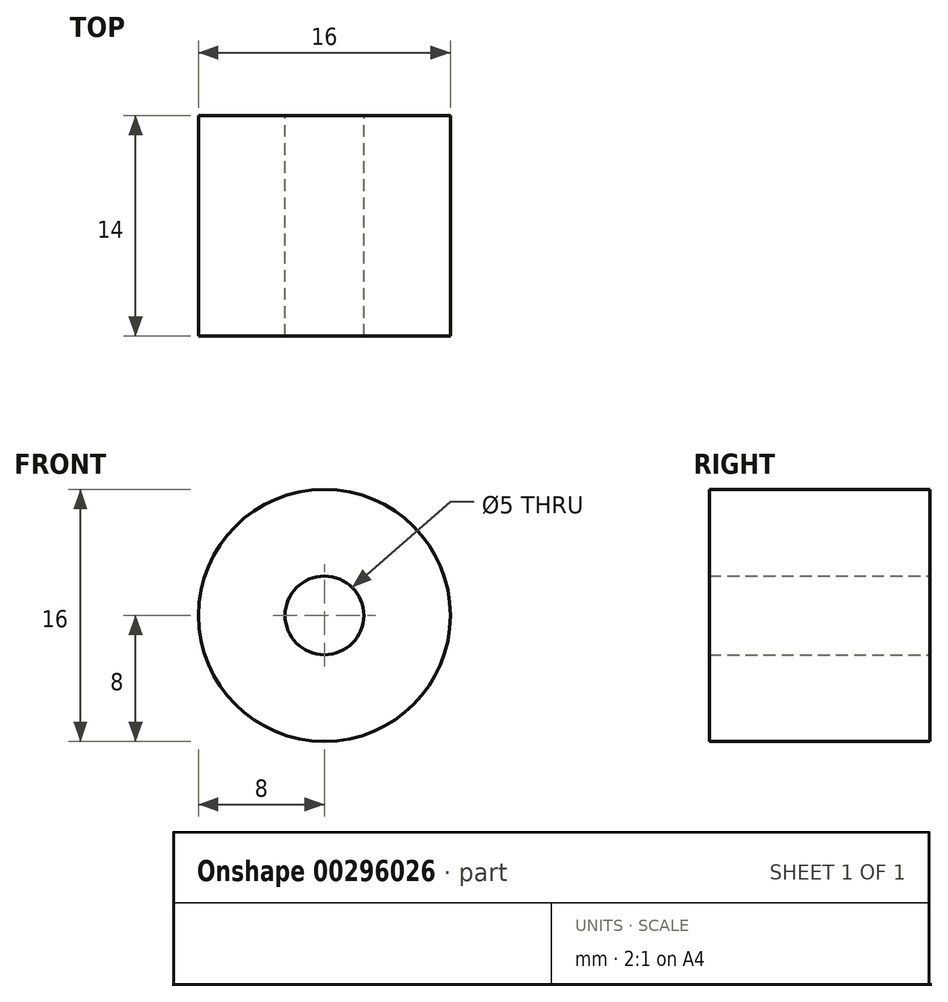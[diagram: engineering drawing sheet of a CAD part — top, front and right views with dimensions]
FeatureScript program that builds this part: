
annotation { "Feature Type Name" : "Feature", "Feature Type Description" : "" }
export const myFeature = defineFeature(function(context is Context, id is Id, definition is map)
    precondition{}
    {
        {
            var Q0;
            Q0=qCreatedBy(makeId("Front.planeOp"),FACE);
            var sketch = newSketch(context, id + "F0", { "sketchPlane" : qUnion([Q0])});
            skCircle(sketch, "E0", {"center": v(0, 0) * mm, "radius": 8 * mm});
            skCircle(sketch, "E1", {"center": v(0, 0) * mm, "radius": 2.5 * mm});
            skSolve(sketch);
        }
        {
            var Q0;
            Q0=makeQuery(id+"F0.imprint","IMPRINT",FACE,{"disambiguationData":[TD([[makeQuery(id+"F0.imprint","IMPRINT",EDGE,{"derivedFrom":sQuery(id+"F0.wireOp",EDGE,"E0")}),1.0]])]});
            extrude(context, id + "F1", {"entities" : qUnion([Q0]), "endBound" : BoundingType.SYMMETRIC, "depth" : 14 * mm});
        }
    });
